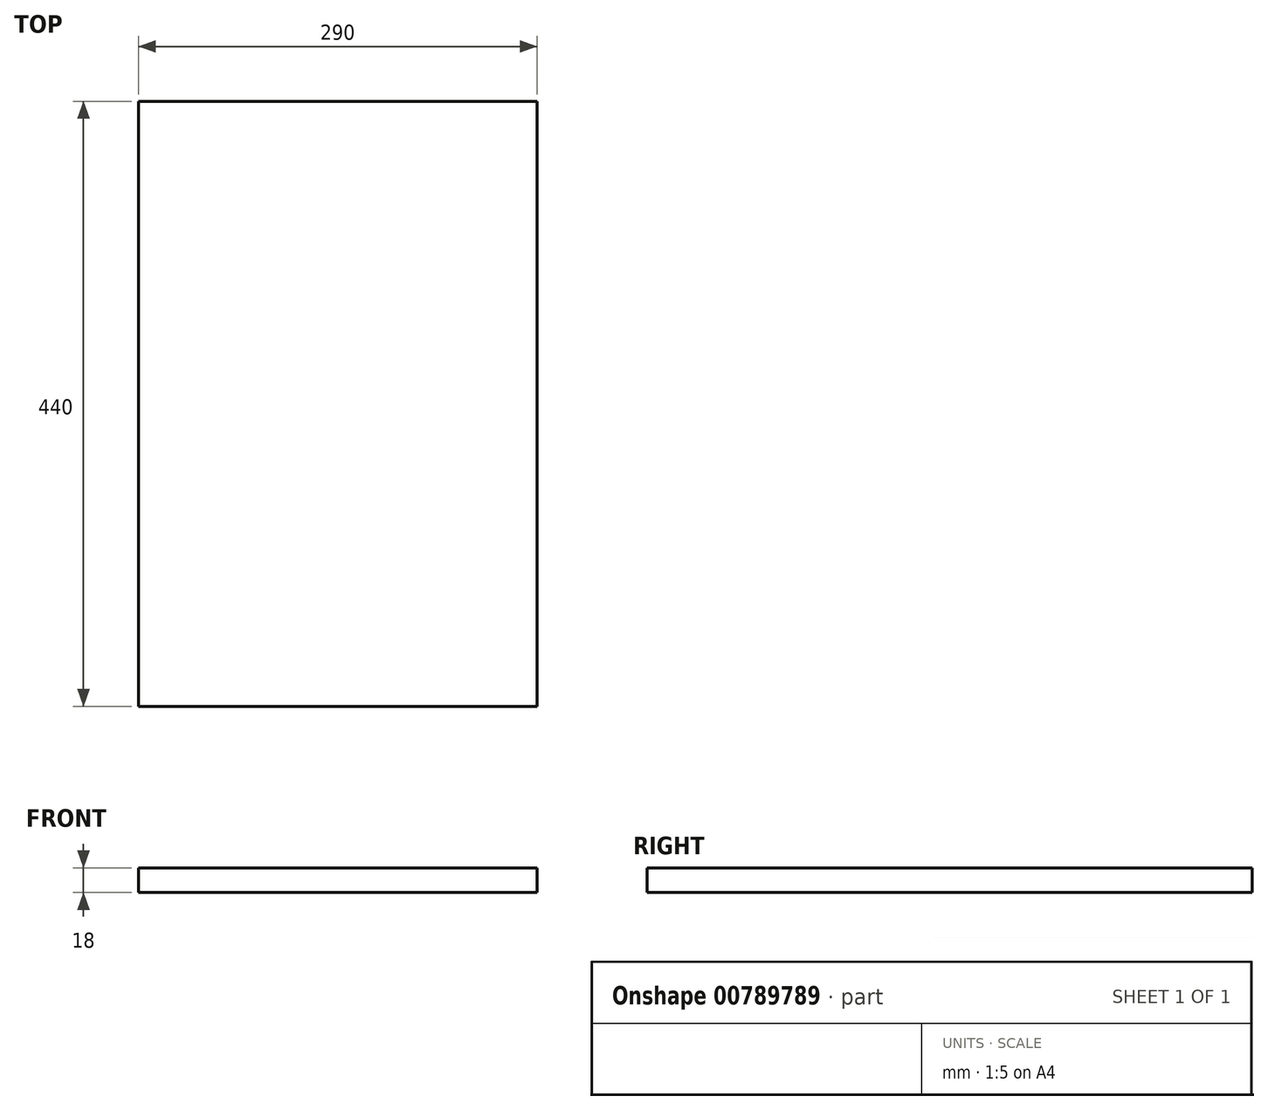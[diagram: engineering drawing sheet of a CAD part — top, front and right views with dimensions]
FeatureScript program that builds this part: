
annotation { "Feature Type Name" : "Feature", "Feature Type Description" : "" }
export const myFeature = defineFeature(function(context is Context, id is Id, definition is map)
    precondition{}
    {
        {
            var Q0;
            Q0=qCreatedBy(makeId("Top.planeOp"),FACE);
            var sketch = newSketch(context, id + "F0", { "sketchPlane" : qUnion([Q0])});
            skLineSegment(sketch, "E0.bottom", {"start": v(-38.72, 372.64) * mm, "end": v(251.28, 372.64) * mm});
            skLineSegment(sketch, "E0.top", {"start": v(-38.72, -67.36) * mm, "end": v(251.28, -67.36) * mm});
            skLineSegment(sketch, "E0.left", {"start": v(-38.72, 372.64) * mm, "end": v(-38.72, -67.36) * mm});
            skLineSegment(sketch, "E0.right", {"start": v(251.28, 372.64) * mm, "end": v(251.28, -67.36) * mm});
            skSolve(sketch);
        }
        {
            var Q0;
            Q0 = qSketchRegion(id + "F0", true);
            extrude(context, id + "F1", {"entities" : qUnion([Q0]), "depth" : 18 * mm, "offsetDistance" : 25 * mm});
        }
    });
